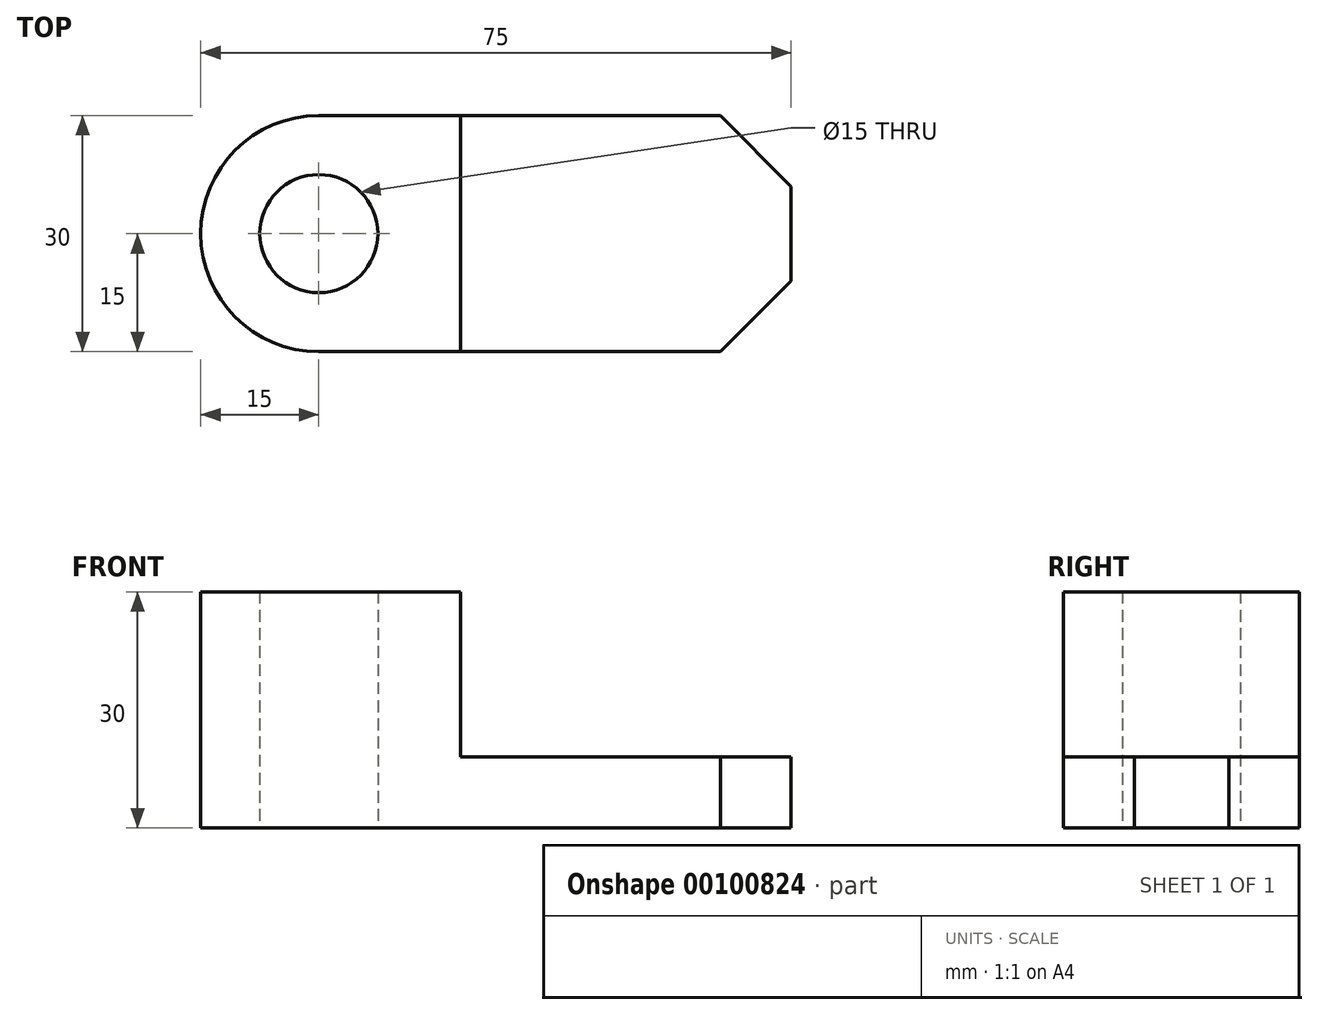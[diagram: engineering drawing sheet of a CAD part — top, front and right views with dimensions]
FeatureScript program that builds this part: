
annotation { "Feature Type Name" : "Feature", "Feature Type Description" : "" }
export const myFeature = defineFeature(function(context is Context, id is Id, definition is map)
    precondition{}
    {
        {
            var Q0;
            Q0=qCreatedBy(makeId("Top.planeOp"),FACE);
            var sketch = newSketch(context, id + "F0", { "sketchPlane" : qUnion([Q0])});
            skLineSegment(sketch, "E0.bottom", {"start": v(0, 0) * mm, "end": v(51, 0) * mm});
            skLineSegment(sketch, "E0.top", {"start": v(0, 30) * mm, "end": v(51, 30) * mm});
            skLineSegment(sketch, "E0.right", {"start": v(60, 9) * mm, "end": v(60, 21) * mm});
            skArc(sketch, "E1", {"start": v(0, 30) * mm, "mid": v(-15, 15) * mm, "end": v(0, 0) * mm});
            skLineSegment(sketch, "E2", {"start": v(0, 30) * mm, "end": v(18, 30) * mm});
            skCircle(sketch, "E3", {"center": v(0, 15) * mm, "radius": 7.5 * mm});
            skLineSegment(sketch, "E4", {"start": v(51, 30) * mm, "end": v(60, 21) * mm});
            skLineSegment(sketch, "E5", {"start": v(60, 9) * mm, "end": v(51, 0) * mm});
            skSolve(sketch);
        }
        {
            var Q0;
            Q0=makeQuery(id+"F0.imprint","IMPRINT",FACE,{"disambiguationData":[TD([[makeQuery(id+"F0.imprint","IMPRINT",EDGE,{"derivedFrom":sQuery(id+"F0.wireOp",EDGE,"E0.bottom")}),1.0]])]});
            extrude(context, id + "F1", {"entities" : qUnion([Q0]), "depth" : 9 * mm});
        }
        {
            var Q0;
            Q0=makeQuery(id+"F1.opExtrude","CAP_FACE",FACE,{"disambiguationData":[OSD([sQuery(id+"F0.wireOp",EDGE,"E0.bottom"),sQuery(id+"F0.wireOp",EDGE,"E0.top"),sQuery(id+"F0.wireOp",EDGE,"E0.right"),sQuery(id+"F0.wireOp",EDGE,"E1"),sQuery(id+"F0.wireOp",EDGE,"E2"),sQuery(id+"F0.wireOp",EDGE,"E3"),sQuery(id+"F0.wireOp",EDGE,"E4"),sQuery(id+"F0.wireOp",EDGE,"E5")])],"isStart":false});
            var sketch = newSketch(context, id + "F2", { "sketchPlane" : qUnion([Q0])});
            skLineSegment(sketch, "E6", {"start": v(0, 0) * mm, "end": v(18, 0) * mm});
            skLineSegment(sketch, "E7", {"start": v(18, 0) * mm, "end": v(18, 30) * mm});
            skSolve(sketch);
        }
        {
            var Q0;
            Q0=makeQuery(id+"F2.imprint","IMPRINT",FACE,{"disambiguationData":[TD([[makeQuery(id+"F2.imprint","IMPRINT",EDGE,{"derivedFrom":sQuery(id+"F2.wireOp",EDGE,"E6")}),1.0]])]});
            extrude(context, id + "F3", {"entities" : qUnion([Q0]), "operationType" : NewBodyOperationType.ADD, "depth" : 21 * mm});
        }
        {
            var Q0;
            Q0=qCreatedBy(makeId("Front.planeOp"),FACE);
            cPlane(context, id + "F4", {"entities" : qUnion([Q0]), "cplaneType" : CPlaneType.OFFSET, "offset" : 15 * mm, "oppositeDirection" : true, "width" : 150 * mm, "height" : 150 * mm});
        }
    });
